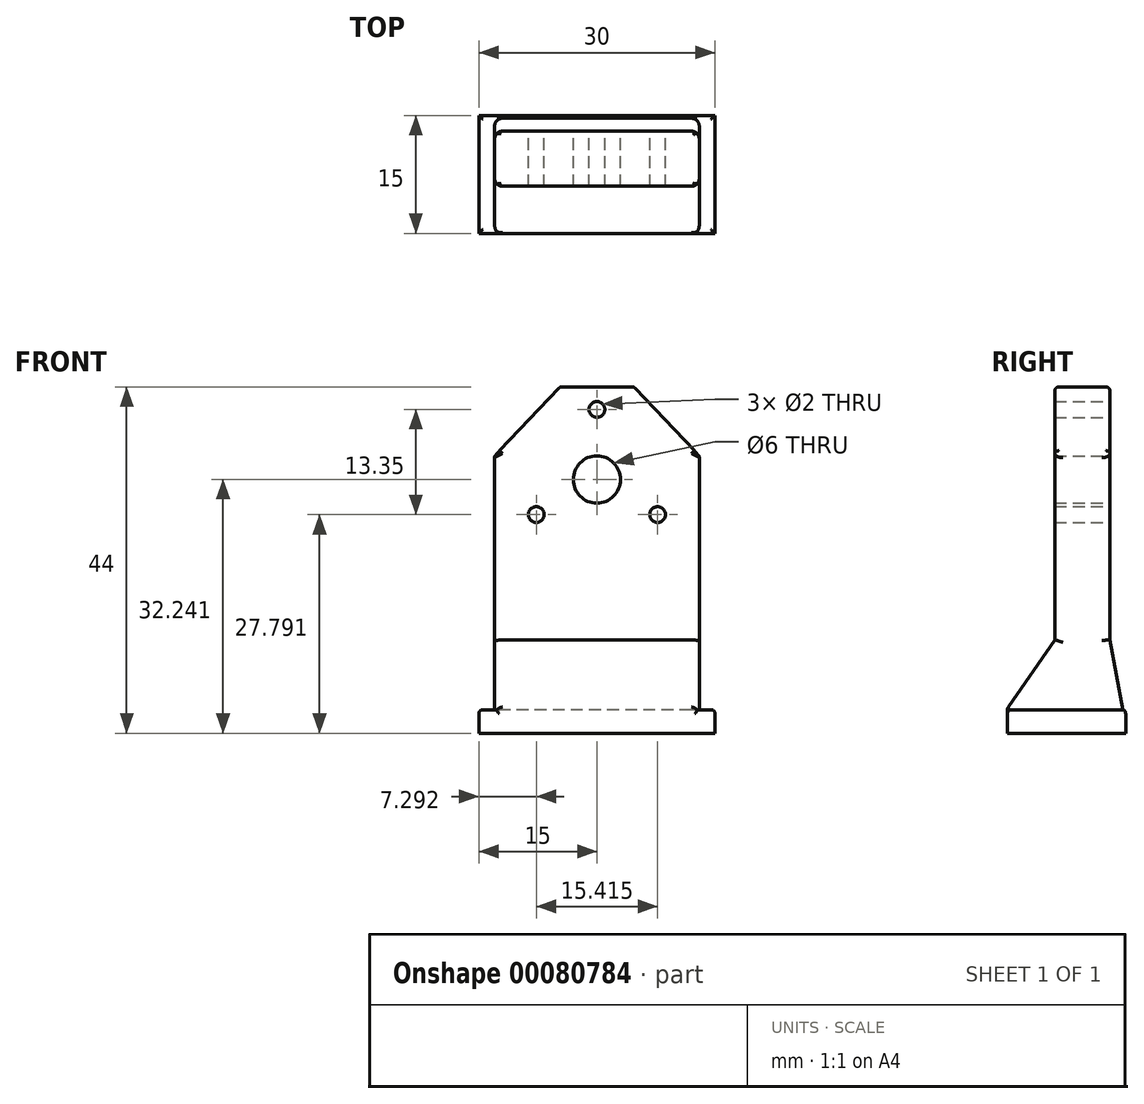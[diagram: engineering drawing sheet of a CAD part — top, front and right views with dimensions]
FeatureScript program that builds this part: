
annotation { "Feature Type Name" : "Feature", "Feature Type Description" : "" }
export const myFeature = defineFeature(function(context is Context, id is Id, definition is map)
    precondition{}
    {
        {
            var Q0;
            Q0=qCreatedBy(makeId("Front.planeOp"),FACE);
            var sketch = newSketch(context, id + "F0", { "sketchPlane" : qUnion([Q0])});
            skLineSegment(sketch, "E0.bottom", {"start": v(-13, 0) * mm, "end": v(13, 0) * mm});
            skLineSegment(sketch, "E0.top", {"start": v(-13, 41) * mm, "end": v(13, 41) * mm});
            skLineSegment(sketch, "E0.left", {"start": v(-13, 0) * mm, "end": v(-13, 41) * mm});
            skLineSegment(sketch, "E0.right", {"start": v(13, 0) * mm, "end": v(13, 41) * mm});
            skPoint(sketch, "E1", {"position": v(0, 0) * mm});
            skCircle(sketch, "E2", {"center": v(0, 29.24) * mm, "radius": 3 * mm});
            skCircle(sketch, "E3", {"center": v(0, 29.24) * mm, "radius": 8.9 * mm, "construction": true});
            skCircle(sketch, "E4", {"center": v(0, 38.14) * mm, "radius": 1 * mm});
            skCircle(sketch, "E5.1.0", {"center": v(-7.7, 24.8) * mm, "radius": 1 * mm});
            skCircle(sketch, "E5.2.0", {"center": v(7.7, 24.8) * mm, "radius": 1 * mm});
            skLineSegment(sketch, "E6", {"start": v(4.7, 41) * mm, "end": v(13, 32.22) * mm});
            skLineSegment(sketch, "E7", {"start": v(0, 0) * mm, "end": v(0, 41) * mm});
            skLineSegment(sketch, "E8.MirrorCS", {"start": v(-4.7, 41) * mm, "end": v(-13, 32.22) * mm});
            skSolve(sketch);
        }
        {
            var Q0;
            Q0=makeQuery(id+"F0.imprint","IMPRINT",FACE,{"disambiguationData":[TD([[makeQuery(id+"F0.imprint","IMPRINT",EDGE,{"derivedFrom":sQuery(id+"F0.wireOp",EDGE,"E0.bottom")}),1.0]])]});
            extrude(context, id + "F1", {"entities" : qUnion([Q0]), "depth" : 7 * mm});
        }
        {
            var Q0;
            Q0=qCreatedBy(makeId("Top.planeOp"),FACE);
            var sketch = newSketch(context, id + "F2", { "sketchPlane" : qUnion([Q0])});
            skLineSegment(sketch, "E9.bottom", {"start": v(-15, 2) * mm, "end": v(15, 2) * mm});
            skLineSegment(sketch, "E9.top", {"start": v(-15, -13) * mm, "end": v(15, -13) * mm});
            skLineSegment(sketch, "E9.left", {"start": v(-15, 2) * mm, "end": v(-15, -13) * mm});
            skLineSegment(sketch, "E9.right", {"start": v(15, 2) * mm, "end": v(15, -13) * mm});
            skSolve(sketch);
        }
        {
            var Q0;
            Q0=makeQuery(id+"F2.imprint","IMPRINT",FACE,{"disambiguationData":[TD([[makeQuery(id+"F2.imprint","IMPRINT",EDGE,{"derivedFrom":sQuery(id+"F2.wireOp",EDGE,"E9.bottom")}),-1.0]])]});
            extrude(context, id + "F3", {"entities" : qUnion([Q0]), "operationType" : NewBodyOperationType.ADD, "oppositeDirection" : true, "depth" : 3 * mm});
        }
        {
            var Q0;
            Q0=makeQuery(id+"F1.opExtrude","SWEPT_FACE",FACE,{"disambiguationData":[OSD([sQuery(id+"F0.wireOp",EDGE,"E0.left")])]});
            var sketch = newSketch(context, id + "F4", { "sketchPlane" : qUnion([Q0])});
            skLineSegment(sketch, "E10", {"start": v(7, 8.88) * mm, "end": v(13.14, 0) * mm});
            skLineSegment(sketch, "E11", {"start": v(7, 6.87) * mm, "end": v(11.75, 0) * mm});
            skLineSegment(sketch, "E12", {"start": v(7, 4.17) * mm, "end": v(9.88, 0) * mm});
            skLineSegment(sketch, "E13", {"start": v(7, 1.96) * mm, "end": v(8.36, 0) * mm});
            skLineSegment(sketch, "E14", {"start": v(7, 4.17) * mm, "end": v(7, 1.96) * mm});
            skLineSegment(sketch, "E15", {"start": v(7, 8.88) * mm, "end": v(7, 6.87) * mm});
            skLineSegment(sketch, "E16", {"start": v(13.14, 0) * mm, "end": v(11.75, 0) * mm});
            skLineSegment(sketch, "E17", {"start": v(9.88, 0) * mm, "end": v(8.36, 0) * mm});
            skLineSegment(sketch, "E18", {"start": v(0, 8.88) * mm, "end": v(-1.63, 0) * mm});
            skLineSegment(sketch, "E19", {"start": v(0, 4.23) * mm, "end": v(-0.78, 0) * mm});
            skLineSegment(sketch, "E20", {"start": v(0, 8.88) * mm, "end": v(0, 4.23) * mm});
            skLineSegment(sketch, "E21", {"start": v(-1.63, 0) * mm, "end": v(-0.78, 0) * mm});
            skLineSegment(sketch, "E22", {"start": v(-0.78, 0) * mm, "end": v(0, 0) * mm});
            skLineSegment(sketch, "E23", {"start": v(0, 0) * mm, "end": v(0, 4.23) * mm});
            skLineSegment(sketch, "E24", {"start": v(7, 6.87) * mm, "end": v(7, 0) * mm});
            skLineSegment(sketch, "E25", {"start": v(7, 0) * mm, "end": v(11.75, 0) * mm});
            skSolve(sketch);
        }
        {
            var Q0;
            Q0 = qSketchRegion(id + "F4", true);
            extrude(context, id + "F5", {"entities" : qUnion([Q0]), "operationType" : NewBodyOperationType.ADD, "oppositeDirection" : true, "depth" : 26 * mm});
        }
        {
            var Q0;
            Q0=makeQuery(id+"F1.opExtrude","CAP_EDGE",EDGE,{"disambiguationData":[OSD([sQuery(id+"F0.wireOp",EDGE,"E6")])],"isStart":false});
            var Q1;
            Q1=makeQuery(id+"F1.opExtrude","CAP_EDGE",EDGE,{"disambiguationData":[OSD([sQuery(id+"F0.wireOp",EDGE,"E0.top")])],"isStart":false});
            var Q2;
            Q2=makeQuery(id+"F1.opExtrude","CAP_EDGE",EDGE,{"disambiguationData":[OSD([sQuery(id+"F0.wireOp",EDGE,"E8.MirrorCS")])],"isStart":true});
            var Q3;
            Q3=makeQuery(id+"F1.opExtrude","CAP_EDGE",EDGE,{"disambiguationData":[OSD([sQuery(id+"F0.wireOp",EDGE,"E8.MirrorCS")])],"isStart":false});
            var Q4;
            Q4=makeQuery(id+"F1.opExtrude","SWEPT_EDGE",EDGE,{"disambiguationData":[OSD([sQuery(id+"F0.wireOp",EDGE,"E0.left"),sQuery(id+"F0.wireOp",EDGE,"E8.MirrorCS")])]});
            var Q5;
            Q5=makeQuery(id+"F1.opExtrude","SWEPT_EDGE",EDGE,{"disambiguationData":[OSD([sQuery(id+"F0.wireOp",EDGE,"E0.top"),sQuery(id+"F0.wireOp",EDGE,"E8.MirrorCS")])]});
            var Q6;
            Q6=makeQuery(id+"F1.opExtrude","SWEPT_EDGE",EDGE,{"disambiguationData":[OSD([sQuery(id+"F0.wireOp",EDGE,"E0.top"),sQuery(id+"F0.wireOp",EDGE,"E6")])]});
            var Q7;
            Q7=makeQuery(id+"F1.opExtrude","CAP_EDGE",EDGE,{"disambiguationData":[OSD([sQuery(id+"F0.wireOp",EDGE,"E0.top")])],"isStart":true});
            var Q8;
            Q8=makeQuery(id+"F1.opExtrude","CAP_EDGE",EDGE,{"disambiguationData":[OSD([sQuery(id+"F0.wireOp",EDGE,"E6")])],"isStart":true});
            var Q9;
            Q9=makeQuery(id+"F1.opExtrude","SWEPT_EDGE",EDGE,{"disambiguationData":[OSD([sQuery(id+"F0.wireOp",EDGE,"E0.right"),sQuery(id+"F0.wireOp",EDGE,"E6")])]});
            fillet(context, id + "F6", {"entities" : qUnion([Q0, Q1, Q2, Q3, Q4, Q5, Q6, Q7, Q8, Q9]), "radius" : 0.5 * mm, "tangentPropagation" : true, "allowEdgeOverflow" : false});
        }
        {
            var Q0;
            Q0=makeQuery(id+"F1.opExtrude","CAP_EDGE",EDGE,{"disambiguationData":[OSD([sQuery(id+"F0.wireOp",EDGE,"E0.right")])],"isStart":false});
            var Q1;
            Q1=makeQuery(id+"F1.opExtrude","CAP_EDGE",EDGE,{"disambiguationData":[OSD([sQuery(id+"F0.wireOp",EDGE,"E0.right")])],"isStart":true});
            var Q2;
            Q2=makeQuery(id+"F5.opExtrude","CAP_EDGE",EDGE,{"disambiguationData":[OSD([sQuery(id+"F4.wireOp",EDGE,"E10")])],"isStart":false});
            var Q3;
            Q3=makeQuery(id+"F5.opExtrude","CAP_EDGE",EDGE,{"disambiguationData":[OSD([sQuery(id+"F4.wireOp",EDGE,"E18")])],"isStart":false});
            var Q4;
            Q4=makeQuery(id+"F1.opExtrude","CAP_EDGE",EDGE,{"disambiguationData":[OSD([sQuery(id+"F0.wireOp",EDGE,"E0.left")])],"isStart":true});
            var Q5;
            Q5=makeQuery(id+"F1.opExtrude","CAP_EDGE",EDGE,{"disambiguationData":[OSD([sQuery(id+"F0.wireOp",EDGE,"E0.left")])],"isStart":false});
            var Q6;
            Q6=makeQuery(id+"F5.opExtrude","CAP_EDGE",EDGE,{"disambiguationData":[OSD([sQuery(id+"F4.wireOp",EDGE,"E18")])],"isStart":true});
            var Q7;
            Q7=makeQuery(id+"F5.opExtrude","CAP_EDGE",EDGE,{"disambiguationData":[OSD([sQuery(id+"F4.wireOp",EDGE,"E10")])],"isStart":true});
            var Q8;
            Q8=makeQuery(id+"F5.opExtrude","SWEPT_EDGE",EDGE,{"disambiguationData":[OSD([sQuery(id+"F0.wireOp",EDGE,"E0.left"),sQuery(id+"F4.wireOp",EDGE,"E10"),sQuery(id+"F4.wireOp",EDGE,"E15")])]});
            fillet(context, id + "F7", {"entities" : qUnion([Q0, Q1, Q2, Q3, Q4, Q5, Q6, Q7, Q8]), "radius" : 1 * mm, "tangentPropagation" : true, "allowEdgeOverflow" : false});
        }
        {
            var Q0;
            Q0=makeQuery(id+"F3.opExtrude","CAP_EDGE",EDGE,{"disambiguationData":[OSD([sQuery(id+"F2.wireOp",EDGE,"E9.left")])],"isStart":true});
            var Q1;
            {var subQ0=sQuery(id+"F2.wireOp",EDGE,"E9.top");var subQ1=makeQuery(id+"F3.opExtrude","SWEPT_FACE",FACE,{"disambiguationData":[OSD([subQ0])]});var subQ2=sQuery(id+"F2.wireOp",EDGE,"E9.left");var subQ3=makeQuery(id+"F3.opExtrude","CAP_FACE",FACE,{"disambiguationData":[OSD([sQuery(id+"F2.wireOp",EDGE,"E9.bottom"),subQ0,subQ2,sQuery(id+"F2.wireOp",EDGE,"E9.right")])],"isStart":true});var subQ4=makeQuery(id+"F1.opExtrude","SWEPT_FACE",FACE,{"disambiguationData":[OSD([sQuery(id+"F0.wireOp",EDGE,"E0.left")])]});var subQ5=sQuery(id+"F4.wireOp",EDGE,"E25");var subQ6=sQuery(id+"F4.wireOp",EDGE,"E24");var subQ7=sQuery(id+"F4.wireOp",EDGE,"E16");var subQ8=sQuery(id+"F4.wireOp",EDGE,"E15");var subQ9=sQuery(id+"F4.wireOp",EDGE,"E10");var subQ10=makeQuery(id+"F5.opExtrude","SWEPT_FACE",FACE,{"disambiguationData":[OSD([subQ7,subQ5])]});var subQ11=makeQuery(id+"F5.opExtrude","CAP_FACE",FACE,{"disambiguationData":[OSD([subQ9,subQ8,subQ7,subQ6,subQ5])],"isStart":true});var subQ12=sQuery(id+"F4.wireOp",EDGE,"E23");var subQ13=sQuery(id+"F4.wireOp",EDGE,"E22");var subQ14=sQuery(id+"F4.wireOp",EDGE,"E21");var subQ15=sQuery(id+"F4.wireOp",EDGE,"E20");var subQ16=sQuery(id+"F4.wireOp",EDGE,"E18");var subQ17=makeQuery(id+"F5.opExtrude","CAP_FACE",FACE,{"disambiguationData":[OSD([subQ16,subQ15,subQ14,subQ13,subQ12])],"isStart":true});var subQ18=makeQuery(id+"F3.opExtrude","CAP_EDGE",EDGE,{"disambiguationData":[OSD([subQ0])],"isStart":true});Q1=makeQuery(id+"F7.opFillet","MERGE",EDGE,{"derivedFrom":[makeQuery(id+"F5.boolean.opBoolean","SPLIT",EDGE,{"disambiguationData":[TD([subQ4,subQ3,subQ1,makeQuery(id+"F3.opExtrude","SWEPT_FACE",FACE,{"disambiguationData":[OSD([subQ2])]}),subQ11,subQ10,subQ17])],"derivedFrom":subQ18}),makeQuery(id+"F5.boolean.opBoolean","SPLIT",EDGE,{"disambiguationData":[TD([subQ4,makeQuery(id+"F1.opExtrude","SWEPT_FACE",FACE,{"disambiguationData":[OSD([sQuery(id+"F0.wireOp",EDGE,"E0.right")])]}),subQ3,subQ1,subQ11,makeQuery(id+"F5.opExtrude","CAP_FACE",FACE,{"disambiguationData":[OSD([subQ9,subQ8,subQ7,subQ6,subQ5])],"isStart":false}),subQ10,subQ17,makeQuery(id+"F5.opExtrude","CAP_FACE",FACE,{"disambiguationData":[OSD([subQ16,subQ15,subQ14,subQ13,subQ12])],"isStart":false})])],"derivedFrom":subQ18})]});}
            var Q2;
            {var subQ0=sQuery(id+"F2.wireOp",EDGE,"E9.top");var subQ1=makeQuery(id+"F3.opExtrude","SWEPT_FACE",FACE,{"disambiguationData":[OSD([subQ0])]});var subQ2=sQuery(id+"F2.wireOp",EDGE,"E9.right");var subQ3=makeQuery(id+"F3.opExtrude","CAP_FACE",FACE,{"disambiguationData":[OSD([sQuery(id+"F2.wireOp",EDGE,"E9.bottom"),subQ0,sQuery(id+"F2.wireOp",EDGE,"E9.left"),subQ2])],"isStart":true});var subQ4=sQuery(id+"F4.wireOp",EDGE,"E25");var subQ5=sQuery(id+"F4.wireOp",EDGE,"E24");var subQ6=sQuery(id+"F4.wireOp",EDGE,"E16");var subQ7=sQuery(id+"F4.wireOp",EDGE,"E15");var subQ8=sQuery(id+"F4.wireOp",EDGE,"E10");var subQ9=makeQuery(id+"F5.opExtrude","CAP_FACE",FACE,{"disambiguationData":[OSD([subQ8,subQ7,subQ6,subQ5,subQ4])],"isStart":false});var subQ10=makeQuery(id+"F1.opExtrude","SWEPT_FACE",FACE,{"disambiguationData":[OSD([sQuery(id+"F0.wireOp",EDGE,"E0.right")])]});var subQ11=makeQuery(id+"F5.opExtrude","SWEPT_FACE",FACE,{"disambiguationData":[OSD([subQ6,subQ4])]});var subQ12=sQuery(id+"F4.wireOp",EDGE,"E23");var subQ13=sQuery(id+"F4.wireOp",EDGE,"E22");var subQ14=sQuery(id+"F4.wireOp",EDGE,"E21");var subQ15=sQuery(id+"F4.wireOp",EDGE,"E20");var subQ16=sQuery(id+"F4.wireOp",EDGE,"E18");var subQ17=makeQuery(id+"F5.opExtrude","CAP_FACE",FACE,{"disambiguationData":[OSD([subQ16,subQ15,subQ14,subQ13,subQ12])],"isStart":false});var subQ18=makeQuery(id+"F3.opExtrude","CAP_EDGE",EDGE,{"disambiguationData":[OSD([subQ0])],"isStart":true});Q2=makeQuery(id+"F7.opFillet","MERGE",EDGE,{"derivedFrom":[makeQuery(id+"F5.boolean.opBoolean","SPLIT",EDGE,{"disambiguationData":[TD([subQ10,subQ3,subQ1,makeQuery(id+"F3.opExtrude","SWEPT_FACE",FACE,{"disambiguationData":[OSD([subQ2])]}),subQ9,subQ11,subQ17])],"derivedFrom":subQ18}),makeQuery(id+"F5.boolean.opBoolean","SPLIT",EDGE,{"disambiguationData":[TD([makeQuery(id+"F1.opExtrude","SWEPT_FACE",FACE,{"disambiguationData":[OSD([sQuery(id+"F0.wireOp",EDGE,"E0.left")])]}),subQ10,subQ3,subQ1,makeQuery(id+"F5.opExtrude","CAP_FACE",FACE,{"disambiguationData":[OSD([subQ8,subQ7,subQ6,subQ5,subQ4])],"isStart":true}),subQ9,subQ11,makeQuery(id+"F5.opExtrude","CAP_FACE",FACE,{"disambiguationData":[OSD([subQ16,subQ15,subQ14,subQ13,subQ12])],"isStart":true}),subQ17])],"derivedFrom":subQ18})]});}
            var Q3;
            Q3=makeQuery(id+"F3.opExtrude","CAP_EDGE",EDGE,{"disambiguationData":[OSD([sQuery(id+"F2.wireOp",EDGE,"E9.right")])],"isStart":true});
            var Q4;
            Q4=makeQuery(id+"F3.opExtrude","CAP_EDGE",EDGE,{"disambiguationData":[OSD([sQuery(id+"F2.wireOp",EDGE,"E9.bottom")])],"isStart":true});
            fillet(context, id + "F8", {"entities" : qUnion([Q0, Q1, Q2, Q3, Q4]), "radius" : 0.5 * mm, "tangentPropagation" : true, "allowEdgeOverflow" : false});
        }
        {
            var Q0;
            Q0=makeQuery(id+"F5.opExtrude","SWEPT_EDGE",EDGE,{"disambiguationData":[OSD([sQuery(id+"F4.wireOp",EDGE,"E10"),sQuery(id+"F4.wireOp",EDGE,"E16")])]});
            var Q1;
            Q1=makeQuery(id+"F7.opFillet","BLEND_EDGE",EDGE,{"blendedFrom":[makeQuery(id+"F5.opExtrude","CAP_EDGE",EDGE,{"disambiguationData":[OSD([sQuery(id+"F4.wireOp",EDGE,"E10")])],"isStart":true}),makeQuery(id+"F5.opExtrude","SWEPT_FACE",FACE,{"disambiguationData":[OSD([sQuery(id+"F4.wireOp",EDGE,"E16"),sQuery(id+"F4.wireOp",EDGE,"E25")])]})],"blendedInto":[makeQuery(id+"F5.opExtrude","SWEPT_FACE",FACE,{"disambiguationData":[OSD([sQuery(id+"F4.wireOp",EDGE,"E16"),sQuery(id+"F4.wireOp",EDGE,"E25")])]})]});
            var Q2;
            {var subQ0=sQuery(id+"F2.wireOp",EDGE,"E9.top");Q2=makeQuery(id+"F8.opFillet","TWEAK_EDGE",EDGE,{"derivedFrom":[makeQuery(id+"F7.opFillet","BLEND_VERTEX",VERTEX,{"blendedFrom":[makeQuery(id+"F5.opExtrude","CAP_EDGE",EDGE,{"disambiguationData":[OSD([sQuery(id+"F4.wireOp",EDGE,"E10")])],"isStart":true}),makeQuery(id+"F3.opExtrude","SWEPT_FACE",FACE,{"disambiguationData":[OSD([subQ0])]}),makeQuery(id+"F3.opExtrude","CAP_FACE",FACE,{"disambiguationData":[OSD([sQuery(id+"F2.wireOp",EDGE,"E9.bottom"),subQ0,sQuery(id+"F2.wireOp",EDGE,"E9.left"),sQuery(id+"F2.wireOp",EDGE,"E9.right")])],"isStart":true}),makeQuery(id+"F5.opExtrude","SWEPT_FACE",FACE,{"disambiguationData":[OSD([sQuery(id+"F4.wireOp",EDGE,"E16"),sQuery(id+"F4.wireOp",EDGE,"E25")])]})],"blendedInto":[makeQuery(id+"F3.opExtrude","SWEPT_FACE",FACE,{"disambiguationData":[OSD([subQ0])]}),makeQuery(id+"F3.opExtrude","CAP_FACE",FACE,{"disambiguationData":[OSD([sQuery(id+"F2.wireOp",EDGE,"E9.bottom"),subQ0,sQuery(id+"F2.wireOp",EDGE,"E9.left"),sQuery(id+"F2.wireOp",EDGE,"E9.right")])],"isStart":true}),makeQuery(id+"F5.opExtrude","SWEPT_FACE",FACE,{"disambiguationData":[OSD([sQuery(id+"F4.wireOp",EDGE,"E16"),sQuery(id+"F4.wireOp",EDGE,"E25")])]})]})]});}
            var Q3;
            {var subQ0=sQuery(id+"F2.wireOp",EDGE,"E9.top");Q3=makeQuery(id+"F8.opFillet","TWEAK_EDGE",EDGE,{"derivedFrom":[makeQuery(id+"F7.opFillet","BLEND_VERTEX",VERTEX,{"blendedFrom":[makeQuery(id+"F5.opExtrude","CAP_EDGE",EDGE,{"disambiguationData":[OSD([sQuery(id+"F4.wireOp",EDGE,"E10")])],"isStart":false}),makeQuery(id+"F3.opExtrude","SWEPT_FACE",FACE,{"disambiguationData":[OSD([subQ0])]}),makeQuery(id+"F3.opExtrude","CAP_FACE",FACE,{"disambiguationData":[OSD([sQuery(id+"F2.wireOp",EDGE,"E9.bottom"),subQ0,sQuery(id+"F2.wireOp",EDGE,"E9.left"),sQuery(id+"F2.wireOp",EDGE,"E9.right")])],"isStart":true}),makeQuery(id+"F5.opExtrude","SWEPT_FACE",FACE,{"disambiguationData":[OSD([sQuery(id+"F4.wireOp",EDGE,"E16"),sQuery(id+"F4.wireOp",EDGE,"E25")])]})],"blendedInto":[makeQuery(id+"F3.opExtrude","SWEPT_FACE",FACE,{"disambiguationData":[OSD([subQ0])]}),makeQuery(id+"F3.opExtrude","CAP_FACE",FACE,{"disambiguationData":[OSD([sQuery(id+"F2.wireOp",EDGE,"E9.bottom"),subQ0,sQuery(id+"F2.wireOp",EDGE,"E9.left"),sQuery(id+"F2.wireOp",EDGE,"E9.right")])],"isStart":true}),makeQuery(id+"F5.opExtrude","SWEPT_FACE",FACE,{"disambiguationData":[OSD([sQuery(id+"F4.wireOp",EDGE,"E16"),sQuery(id+"F4.wireOp",EDGE,"E25")])]})]})]});}
            var Q4;
            Q4=makeQuery(id+"F7.opFillet","BLEND_EDGE",EDGE,{"blendedFrom":[makeQuery(id+"F5.opExtrude","CAP_EDGE",EDGE,{"disambiguationData":[OSD([sQuery(id+"F4.wireOp",EDGE,"E10")])],"isStart":false}),makeQuery(id+"F5.opExtrude","SWEPT_FACE",FACE,{"disambiguationData":[OSD([sQuery(id+"F4.wireOp",EDGE,"E16"),sQuery(id+"F4.wireOp",EDGE,"E25")])]})],"blendedInto":[makeQuery(id+"F5.opExtrude","SWEPT_FACE",FACE,{"disambiguationData":[OSD([sQuery(id+"F4.wireOp",EDGE,"E16"),sQuery(id+"F4.wireOp",EDGE,"E25")])]})]});
            fillet(context, id + "F9", {"entities" : qUnion([Q0, Q1, Q2, Q3, Q4]), "radius" : 0.5 * mm, "tangentPropagation" : true, "allowEdgeOverflow" : false});
        }
    });
